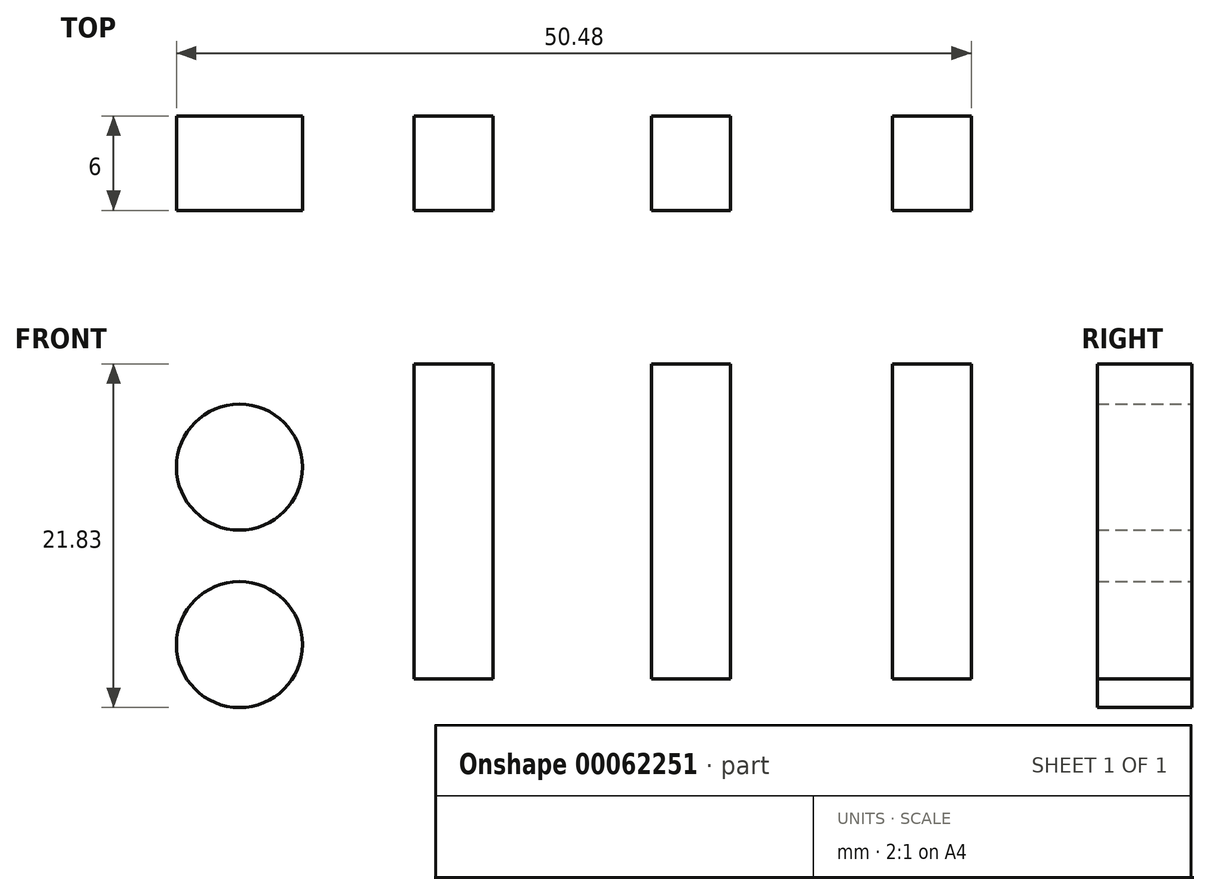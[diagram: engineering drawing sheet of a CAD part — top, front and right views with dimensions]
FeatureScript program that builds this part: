
annotation { "Feature Type Name" : "Feature", "Feature Type Description" : "" }
export const myFeature = defineFeature(function(context is Context, id is Id, definition is map)
    precondition{}
    {
        {
            var Q0;
            Q0=qCreatedBy(makeId("Front.planeOp"),FACE);
            var sketch = newSketch(context, id + "F0", { "sketchPlane" : qUnion([Q0])});
            skLineSegment(sketch, "E0.bottom", {"start": v(-43.63, 32.52) * mm, "end": v(-38.63, 32.52) * mm});
            skLineSegment(sketch, "E0.top", {"start": v(-43.63, 12.52) * mm, "end": v(-38.63, 12.52) * mm});
            skLineSegment(sketch, "E0.left", {"start": v(-43.63, 32.52) * mm, "end": v(-43.63, 12.52) * mm});
            skLineSegment(sketch, "E0.right", {"start": v(-38.63, 32.52) * mm, "end": v(-38.63, 12.52) * mm});
            skCircle(sketch, "E1", {"center": v(-54.72, 25.96) * mm, "radius": 4 * mm});
            skLineSegment(sketch, "E2.bottom", {"start": v(-28.55, 32.52) * mm, "end": v(-23.55, 32.52) * mm});
            skLineSegment(sketch, "E2.top", {"start": v(-28.55, 12.52) * mm, "end": v(-23.55, 12.52) * mm});
            skLineSegment(sketch, "E2.left", {"start": v(-28.55, 32.52) * mm, "end": v(-28.55, 12.52) * mm});
            skLineSegment(sketch, "E2.right", {"start": v(-23.55, 32.52) * mm, "end": v(-23.55, 12.52) * mm});
            skLineSegment(sketch, "E3.bottom", {"start": v(-13.24, 32.52) * mm, "end": v(-8.24, 32.52) * mm});
            skLineSegment(sketch, "E3.top", {"start": v(-13.24, 12.52) * mm, "end": v(-8.24, 12.52) * mm});
            skLineSegment(sketch, "E3.left", {"start": v(-13.24, 32.52) * mm, "end": v(-13.24, 12.52) * mm});
            skLineSegment(sketch, "E3.right", {"start": v(-8.24, 32.52) * mm, "end": v(-8.24, 12.52) * mm});
            skCircle(sketch, "E4", {"center": v(-54.72, 14.7) * mm, "radius": 4 * mm});
            skSolve(sketch);
        }
        {
            var Q0;
            Q0 = qSketchRegion(id + "F0", true);
            extrude(context, id + "F1", {"entities" : qUnion([Q0]), "depth" : 6 * mm});
        }
    });
